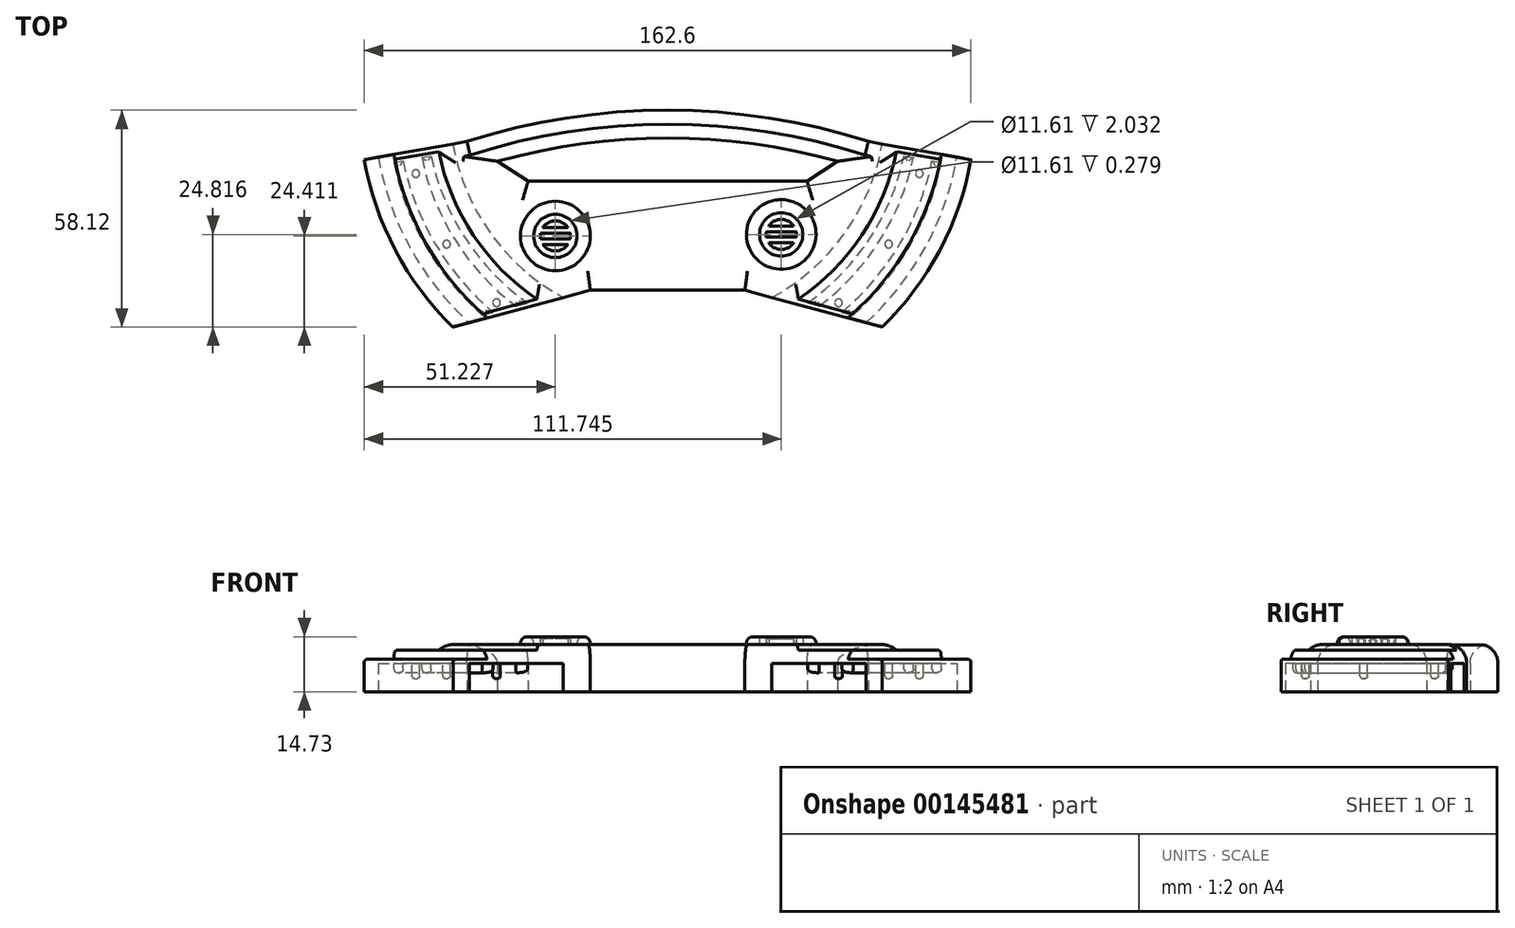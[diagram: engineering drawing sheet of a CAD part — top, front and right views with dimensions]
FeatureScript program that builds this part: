
annotation { "Feature Type Name" : "Feature", "Feature Type Description" : "" }
export const myFeature = defineFeature(function(context is Context, id is Id, definition is map)
    precondition{}
    {
        {
            var Q0;
            Q0=qCreatedBy(makeId("Top.planeOp"),FACE);
            var sketch = newSketch(context, id + "F0", { "sketchPlane" : qUnion([Q0])});
            skCircle(sketch, "E0", {"center": v(0, 0) * mm, "radius": 76.2 * mm, "construction": true});
            skCircle(sketch, "E1", {"center": v(0, 0) * mm, "radius": 60.96 * mm, "construction": true});
            skArc(sketch, "E2", {"start": v(-81.3, -14.33) * mm, "mid": v(-72.94, -38.65) * mm, "end": v(-57.5, -59.22) * mm});
            skLineSegment(sketch, "E3", {"start": v(0, 0) * mm, "end": v(-81.3, -14.33) * mm, "construction": true});
            skArc(sketch, "E4", {"start": v(81.3, -14.33) * mm, "mid": v(72.94, -38.65) * mm, "end": v(57.5, -59.22) * mm});
            skLineSegment(sketch, "E5", {"start": v(81.3, -14.33) * mm, "end": v(0, 0) * mm, "construction": true});
            skLineSegment(sketch, "E6", {"start": v(81.3, -14.33) * mm, "end": v(57.5, -59.22) * mm, "construction": true});
            skLineSegment(sketch, "E7", {"start": v(-81.3, -14.33) * mm, "end": v(-57.5, -59.22) * mm, "construction": true});
            skLineSegment(sketch, "E8", {"start": v(57.5, -59.22) * mm, "end": v(20.7, -49.36) * mm});
            skLineSegment(sketch, "E9", {"start": v(20.7, -49.36) * mm, "end": v(-20.7, -49.36) * mm});
            skLineSegment(sketch, "E10", {"start": v(-20.7, -49.36) * mm, "end": v(-57.5, -59.22) * mm});
            skLineSegment(sketch, "E11", {"start": v(-81.3, -14.33) * mm, "end": v(-53.78, -9.48) * mm});
            skLineSegment(sketch, "E12", {"start": v(-45.58, -14.8) * mm, "end": v(-37.38, -20.13) * mm});
            skLineSegment(sketch, "E13", {"start": v(-37.38, -20.13) * mm, "end": v(37.38, -20.13) * mm});
            skLineSegment(sketch, "E14", {"start": v(37.38, -20.13) * mm, "end": v(45.58, -14.8) * mm});
            skLineSegment(sketch, "E15", {"start": v(53.78, -9.48) * mm, "end": v(81.3, -14.33) * mm});
            skLineSegment(sketch, "E16", {"start": v(0, 0) * mm, "end": v(0, -177.8) * mm, "construction": true});
            skArc(sketch, "E17", {"start": v(-53.78, -9.48) * mm, "mid": v(0, -1.1) * mm, "end": v(53.78, -9.48) * mm});
            skArc(sketch, "E18", {"start": v(45.58, -14.8) * mm, "mid": v(0, -8.56) * mm, "end": v(-45.58, -14.8) * mm});
            skSolve(sketch);
        }
        {
            var Q0;
            Q0=qSketchRegion(id+"F0",true);
            extrude(context, id + "F1", {"entities" : qUnion([Q0]), "depth" : 12.7 * mm});
        }
        {
            var Q0;
            Q0=qCreatedBy(makeId("Front.planeOp"),FACE);
            var sketch = newSketch(context, id + "F2", { "sketchPlane" : qUnion([Q0])});
            skLineSegment(sketch, "E19", {"start": v(62.5, 16.37) * mm, "end": v(62.5, 11.1) * mm});
            skLineSegment(sketch, "E20", {"start": v(62.5, 11.1) * mm, "end": v(74.5, 11.1) * mm});
            skLineSegment(sketch, "E21", {"start": v(74.5, 11.1) * mm, "end": v(74.5, 8.65) * mm});
            skLineSegment(sketch, "E22", {"start": v(74.5, 8.65) * mm, "end": v(83.99, 8.65) * mm});
            skLineSegment(sketch, "E23", {"start": v(83.99, 8.65) * mm, "end": v(83.99, 15.75) * mm});
            skLineSegment(sketch, "E24", {"start": v(83.99, 15.75) * mm, "end": v(62.5, 16.37) * mm});
            skSolve(sketch);
        }
        {
            var Q0;
            Q0=qCreatedBy(makeId("Front.planeOp"),FACE);
            var sketch = newSketch(context, id + "F3", { "sketchPlane" : qUnion([Q0])});
            skLineSegment(sketch, "E25", {"start": v(0, 99.5) * mm, "end": v(0, -112.08) * mm, "construction": true});
            skSolve(sketch);
        }
        {
            var Q0;
            Q0=qSketchRegion(id+"F2",true);
            var Q1;
            Q1=sQuery(id+"F3.wireOp",EDGE,"E25");
            revolve(context, id + "F4", {"operationType" : NewBodyOperationType.REMOVE, "entities" : qUnion([Q0]), "axis" : qUnion([Q1]), "revolveType" : RevolveType.FULL, "oppositeDirection" : true});
        }
        {
            var Q0;
            Q0=makeQuery(id+"F1.opExtrude","CAP_FACE",FACE,{"disambiguationData":[OSD([sQuery(id+"F0.wireOp",EDGE,"E2"),sQuery(id+"F0.wireOp",EDGE,"E4"),sQuery(id+"F0.wireOp",EDGE,"E8"),sQuery(id+"F0.wireOp",EDGE,"E9"),sQuery(id+"F0.wireOp",EDGE,"E10"),sQuery(id+"F0.wireOp",EDGE,"E11"),sQuery(id+"F0.wireOp",EDGE,"E12"),sQuery(id+"F0.wireOp",EDGE,"E13"),sQuery(id+"F0.wireOp",EDGE,"E14"),sQuery(id+"F0.wireOp",EDGE,"E15"),sQuery(id+"F0.wireOp",EDGE,"E17"),sQuery(id+"F0.wireOp",EDGE,"E18")])],"isStart":false});
            fillet(context, id + "F5", {"entities" : qUnion([Q0]), "radius" : 5.08 * mm, "tangentPropagation" : true, "allowEdgeOverflow" : false});
        }
        {
            var Q0;
            Q0=makeQuery(id+"F1.opExtrude","CAP_FACE",FACE,{"disambiguationData":[OSD([sQuery(id+"F0.wireOp",EDGE,"E2"),sQuery(id+"F0.wireOp",EDGE,"E4"),sQuery(id+"F0.wireOp",EDGE,"E8"),sQuery(id+"F0.wireOp",EDGE,"E9"),sQuery(id+"F0.wireOp",EDGE,"E10"),sQuery(id+"F0.wireOp",EDGE,"E11"),sQuery(id+"F0.wireOp",EDGE,"E12"),sQuery(id+"F0.wireOp",EDGE,"E13"),sQuery(id+"F0.wireOp",EDGE,"E14"),sQuery(id+"F0.wireOp",EDGE,"E15"),sQuery(id+"F0.wireOp",EDGE,"E17"),sQuery(id+"F0.wireOp",EDGE,"E18")])],"isStart":false});
            var sketch = newSketch(context, id + "F6", { "sketchPlane" : qUnion([Q0])});
            skLineSegment(sketch, "E26", {"start": v(38.88, -25.21) * mm, "end": v(34.33, -47.75) * mm, "construction": true});
            skLineSegment(sketch, "E27", {"start": v(34.33, -47.75) * mm, "end": v(56.82, -15.18) * mm, "construction": true});
            skLineSegment(sketch, "E28", {"start": v(56.82, -15.18) * mm, "end": v(-56.82, -15.18) * mm, "construction": true});
            skLineSegment(sketch, "E29", {"start": v(-56.82, -15.18) * mm, "end": v(-34.33, -47.75) * mm, "construction": true});
            skLineSegment(sketch, "E30", {"start": v(-34.33, -47.75) * mm, "end": v(-38.88, -25.21) * mm, "construction": true});
            skLineSegment(sketch, "E31", {"start": v(-38.88, -25.21) * mm, "end": v(46.13, -36.48) * mm, "construction": true});
            skPoint(sketch, "E31.endSnap0", {"position": v(-36.6, -36.48) * mm});
            skLineSegment(sketch, "E32", {"start": v(46.13, -36.48) * mm, "end": v(-42.1, -36.48) * mm, "construction": true});
            skLineSegment(sketch, "E33", {"start": v(-42.1, -36.48) * mm, "end": v(38.88, -25.21) * mm, "construction": true});
            skLineSegment(sketch, "E34", {"start": v(21.38, -44.28) * mm, "end": v(38.88, -25.21) * mm, "construction": true});
            skLineSegment(sketch, "E35", {"start": v(-21.38, -44.28) * mm, "end": v(-38.88, -25.21) * mm, "construction": true});
            skCircle(sketch, "E36", {"center": v(30.44, -34.4) * mm, "radius": 9.33 * mm});
            skCircle(sketch, "E37", {"center": v(-30.07, -34.8) * mm, "radius": 9.33 * mm});
            skCircle(sketch, "E38", {"center": v(-30.07, -34.8) * mm, "radius": 5.8 * mm});
            skCircle(sketch, "E39", {"center": v(30.44, -34.4) * mm, "radius": 5.8 * mm});
            skSolve(sketch);
        }
        {
            var Q0;
            Q0=qSketchRegion(id+"F6",true);
            extrude(context, id + "F7", {"entities" : qUnion([Q0]), "operationType" : NewBodyOperationType.ADD, "depth" : 2.03 * mm});
        }
        {
            var Q0;
            Q0=makeQuery(id+"F7.opExtrude","CAP_FACE",FACE,{"disambiguationData":[OSD([sQuery(id+"F6.wireOp",EDGE,"E37"),sQuery(id+"F6.wireOp",EDGE,"E38")])],"isStart":false});
            var Q1;
            Q1=makeQuery(id+"F7.opExtrude","CAP_EDGE",EDGE,{"disambiguationData":[OSD([sQuery(id+"F6.wireOp",EDGE,"E36")])],"isStart":false});
            fillet(context, id + "F8", {"entities" : qUnion([Q0, Q1]), "radius" : 1.75 * mm, "tangentPropagation" : true, "allowEdgeOverflow" : false});
        }
        {
            var Q0;
            Q0=makeQuery(id+"F7.boolean.opBoolean","SPLIT",FACE,{"disambiguationData":[TD([makeQuery(id+"F7.opExtrude","SWEPT_FACE",FACE,{"disambiguationData":[OSD([sQuery(id+"F6.wireOp",EDGE,"E38")])]})])],"derivedFrom":makeQuery(id+"F1.opExtrude","CAP_FACE",FACE,{"disambiguationData":[OSD([sQuery(id+"F0.wireOp",EDGE,"E2"),sQuery(id+"F0.wireOp",EDGE,"E4"),sQuery(id+"F0.wireOp",EDGE,"E8"),sQuery(id+"F0.wireOp",EDGE,"E9"),sQuery(id+"F0.wireOp",EDGE,"E10"),sQuery(id+"F0.wireOp",EDGE,"E11"),sQuery(id+"F0.wireOp",EDGE,"E12"),sQuery(id+"F0.wireOp",EDGE,"E13"),sQuery(id+"F0.wireOp",EDGE,"E14"),sQuery(id+"F0.wireOp",EDGE,"E15"),sQuery(id+"F0.wireOp",EDGE,"E17"),sQuery(id+"F0.wireOp",EDGE,"E18")])],"isStart":false})});
            var sketch = newSketch(context, id + "F9", { "sketchPlane" : qUnion([Q0])});
            skArc(sketch, "E40", {"start": v(-34.04, -34.07) * mm, "mid": v(-34.11, -34.8) * mm, "end": v(-34.04, -35.55) * mm});
            skLineSegment(sketch, "E41", {"start": v(-26.73, -32.55) * mm, "end": v(-33.42, -32.55) * mm});
            skLineSegment(sketch, "E42", {"start": v(-26.1, -34.07) * mm, "end": v(-34.04, -34.07) * mm});
            skLineSegment(sketch, "E43", {"start": v(-26.1, -35.55) * mm, "end": v(-34.04, -35.55) * mm});
            skLineSegment(sketch, "E44", {"start": v(-33.42, -37.07) * mm, "end": v(-26.73, -37.07) * mm});
            skArc(sketch, "E45.trimOffspring", {"start": v(-26.73, -32.55) * mm, "mid": v(-30.07, -30.77) * mm, "end": v(-33.42, -32.55) * mm});
            skArc(sketch, "E46.trimOffspring", {"start": v(-26.1, -35.55) * mm, "mid": v(-26.03, -34.8) * mm, "end": v(-26.1, -34.07) * mm});
            skArc(sketch, "E47.trimOffspring", {"start": v(-33.42, -37.07) * mm, "mid": v(-30.07, -38.85) * mm, "end": v(-26.73, -37.07) * mm});
            skSolve(sketch);
        }
        {
            var Q0;
            Q0=makeQuery(id+"F7.boolean.opBoolean","SPLIT",FACE,{"disambiguationData":[TD([makeQuery(id+"F7.opExtrude","SWEPT_FACE",FACE,{"disambiguationData":[OSD([sQuery(id+"F6.wireOp",EDGE,"E39")])]})])],"derivedFrom":makeQuery(id+"F1.opExtrude","CAP_FACE",FACE,{"disambiguationData":[OSD([sQuery(id+"F0.wireOp",EDGE,"E2"),sQuery(id+"F0.wireOp",EDGE,"E4"),sQuery(id+"F0.wireOp",EDGE,"E8"),sQuery(id+"F0.wireOp",EDGE,"E9"),sQuery(id+"F0.wireOp",EDGE,"E10"),sQuery(id+"F0.wireOp",EDGE,"E11"),sQuery(id+"F0.wireOp",EDGE,"E12"),sQuery(id+"F0.wireOp",EDGE,"E13"),sQuery(id+"F0.wireOp",EDGE,"E14"),sQuery(id+"F0.wireOp",EDGE,"E15"),sQuery(id+"F0.wireOp",EDGE,"E17"),sQuery(id+"F0.wireOp",EDGE,"E18")])],"isStart":false})});
            var sketch = newSketch(context, id + "F10", { "sketchPlane" : qUnion([Q0])});
            skArc(sketch, "E48", {"start": v(33.8, -32.14) * mm, "mid": v(30.44, -30.37) * mm, "end": v(27.1, -32.14) * mm});
            skLineSegment(sketch, "E49", {"start": v(27.1, -32.14) * mm, "end": v(33.8, -32.14) * mm});
            skLineSegment(sketch, "E50", {"start": v(34.42, -33.67) * mm, "end": v(26.47, -33.67) * mm});
            skLineSegment(sketch, "E51", {"start": v(26.47, -35.14) * mm, "end": v(34.42, -35.14) * mm});
            skLineSegment(sketch, "E52", {"start": v(33.8, -36.67) * mm, "end": v(27.1, -36.67) * mm});
            skArc(sketch, "E53.trimOffspring", {"start": v(26.47, -33.67) * mm, "mid": v(26.4, -34.4) * mm, "end": v(26.47, -35.14) * mm});
            skArc(sketch, "E54.trimOffspring", {"start": v(27.1, -36.67) * mm, "mid": v(30.44, -38.44) * mm, "end": v(33.8, -36.67) * mm});
            skArc(sketch, "E55.trimOffspring", {"start": v(34.42, -35.14) * mm, "mid": v(34.48, -34.4) * mm, "end": v(34.42, -33.67) * mm});
            skSolve(sketch);
        }
        {
            var Q0;
            Q0=qSketchRegion(id+"F9",true);
            extrude(context, id + "F11", {"entities" : qUnion([Q0]), "operationType" : NewBodyOperationType.ADD, "depth" : 1.52 * mm});
        }
        {
            var Q0;
            Q0=makeQuery(id+"F11.opExtrude","CAP_EDGE",EDGE,{"disambiguationData":[OSD([sQuery(id+"F9.wireOp",EDGE,"E42")])],"isStart":false});
            var Q1;
            Q1=makeQuery(id+"F11.opExtrude","CAP_EDGE",EDGE,{"disambiguationData":[OSD([sQuery(id+"F9.wireOp",EDGE,"E43")])],"isStart":false});
            fillet(context, id + "F12", {"entities" : qUnion([Q0, Q1]), "radius" : 0.7 * mm, "tangentPropagation" : true, "allowEdgeOverflow" : false});
        }
        {
            var Q0;
            Q0=makeQuery(id+"F11.opExtrude","CAP_FACE",FACE,{"disambiguationData":[OSD([sQuery(id+"F9.wireOp",EDGE,"E41"),sQuery(id+"F9.wireOp",EDGE,"E45.trimOffspring")])],"isStart":false});
            var Q1;
            Q1=makeQuery(id+"F11.opExtrude","CAP_FACE",FACE,{"disambiguationData":[OSD([sQuery(id+"F9.wireOp",EDGE,"E44"),sQuery(id+"F9.wireOp",EDGE,"E47.trimOffspring")])],"isStart":false});
            fillet(context, id + "F13", {"entities" : qUnion([Q0, Q1]), "radius" : 0.25 * mm, "tangentPropagation" : true, "allowEdgeOverflow" : false});
        }
        {
            var Q0;
            Q0=qSketchRegion(id+"F10",true);
            extrude(context, id + "F14", {"entities" : qUnion([Q0]), "operationType" : NewBodyOperationType.ADD, "depth" : 1.52 * mm});
        }
        {
            var Q0;
            {var subQ0=sQuery(id+"F2.wireOp",EDGE,"E20");var subQ1=sQuery(id+"F2.wireOp",EDGE,"E21");Q0=makeQuery(id+"F4.boolean.opBoolean","COPY",EDGE,{"disambiguationData":[TD([makeQuery(id+"F1.opExtrude","SWEPT_FACE",FACE,{"disambiguationData":[OSD([sQuery(id+"F0.wireOp",EDGE,"E10")])]})])],"derivedFrom":makeQuery(id+"F4.opRevolve","SWEPT_EDGE",EDGE,{"disambiguationData":[OSD([subQ0,subQ1])]})});}
            var Q1;
            Q1=makeQuery(id+"F4.boolean.opBoolean","INTERSECT",EDGE,{"derivedFrom":[makeQuery(id+"F1.opExtrude","SWEPT_FACE",FACE,{"disambiguationData":[OSD([sQuery(id+"F0.wireOp",EDGE,"E2")])]}),makeQuery(id+"F4.opRevolve","SWEPT_FACE",FACE,{"disambiguationData":[OSD([sQuery(id+"F2.wireOp",EDGE,"E22")])]})]});
            var Q2;
            {var subQ0=sQuery(id+"F2.wireOp",EDGE,"E20");var subQ1=sQuery(id+"F2.wireOp",EDGE,"E21");Q2=makeQuery(id+"F4.boolean.opBoolean","COPY",EDGE,{"disambiguationData":[TD([makeQuery(id+"F1.opExtrude","SWEPT_FACE",FACE,{"disambiguationData":[OSD([sQuery(id+"F0.wireOp",EDGE,"E8")])]})])],"derivedFrom":makeQuery(id+"F4.opRevolve","SWEPT_EDGE",EDGE,{"disambiguationData":[OSD([subQ0,subQ1])]})});}
            var Q3;
            Q3=makeQuery(id+"F4.boolean.opBoolean","INTERSECT",EDGE,{"derivedFrom":[makeQuery(id+"F1.opExtrude","SWEPT_FACE",FACE,{"disambiguationData":[OSD([sQuery(id+"F0.wireOp",EDGE,"E4")])]}),makeQuery(id+"F4.opRevolve","SWEPT_FACE",FACE,{"disambiguationData":[OSD([sQuery(id+"F2.wireOp",EDGE,"E22")])]})]});
            fillet(context, id + "F15", {"entities" : qUnion([Q0, Q1, Q2, Q3]), "radius" : 0.76 * mm, "tangentPropagation" : true, "allowEdgeOverflow" : false});
        }
        {
            var Q0;
            Q0=qCreatedBy(makeId("Top.planeOp"),FACE);
            var sketch = newSketch(context, id + "F16", { "sketchPlane" : qUnion([Q0])});
            skCircle(sketch, "E56", {"center": v(0, 0) * mm, "radius": 78.74 * mm});
            skCircle(sketch, "E57", {"center": v(0, 0) * mm, "radius": 58.42 * mm});
            skSolve(sketch);
        }
        {
            var Q0;
            Q0=qSketchRegion(id+"F16",true);
            extrude(context, id + "F17", {"entities" : qUnion([Q0]), "operationType" : NewBodyOperationType.REMOVE, "depth" : 7.62 * mm});
        }
        {
            var Q0;
            Q0=makeQuery(id+"F14.opExtrude","CAP_EDGE",EDGE,{"disambiguationData":[OSD([sQuery(id+"F10.wireOp",EDGE,"E50")])],"isStart":false});
            var Q1;
            Q1=makeQuery(id+"F14.opExtrude","CAP_EDGE",EDGE,{"disambiguationData":[OSD([sQuery(id+"F10.wireOp",EDGE,"E51")])],"isStart":false});
            fillet(context, id + "F18", {"entities" : qUnion([Q0, Q1]), "radius" : 0.71 * mm, "tangentPropagation" : true, "allowEdgeOverflow" : false});
        }
        {
            var Q0;
            Q0=makeQuery(id+"F14.opExtrude","CAP_FACE",FACE,{"disambiguationData":[OSD([sQuery(id+"F10.wireOp",EDGE,"E48"),sQuery(id+"F10.wireOp",EDGE,"E49")])],"isStart":false});
            var Q1;
            Q1=makeQuery(id+"F14.opExtrude","CAP_FACE",FACE,{"disambiguationData":[OSD([sQuery(id+"F10.wireOp",EDGE,"E52"),sQuery(id+"F10.wireOp",EDGE,"E54.trimOffspring")])],"isStart":false});
            fillet(context, id + "F19", {"entities" : qUnion([Q0, Q1]), "radius" : 0.25 * mm, "tangentPropagation" : true, "allowEdgeOverflow" : false});
        }
        {
            var Q0;
            {var subQ1=sQuery(id+"F0.wireOp",EDGE,"E10");var subQ2=sQuery(id+"F16.wireOp",EDGE,"E56");var subQ3=sQuery(id+"F16.wireOp",EDGE,"E57");Q0=makeQuery(id+"F17.boolean.opBoolean","COPY",FACE,{"disambiguationData":[TD([makeQuery(id+"F1.opExtrude","SWEPT_FACE",FACE,{"disambiguationData":[OSD([subQ1])]})])],"derivedFrom":makeQuery(id+"F17.opExtrude","CAP_FACE",FACE,{"disambiguationData":[OSD([subQ2,subQ3])],"isStart":false})});}
            var sketch = newSketch(context, id + "F20", { "sketchPlane" : qUnion([Q0])});
            skCircle(sketch, "E58", {"center": v(0, 0) * mm, "radius": 76.2 * mm, "construction": true});
            skCircle(sketch, "E59", {"center": v(0, 0) * mm, "radius": 60.96 * mm, "construction": true});
            skLineSegment(sketch, "E60", {"start": v(0, 0) * mm, "end": v(67.47, 18.08) * mm, "construction": true});
            skCircle(sketch, "E61", {"center": v(0, 0) * mm, "radius": 69.85 * mm, "construction": true});
            skLineSegment(sketch, "E62", {"start": v(0, 0) * mm, "end": v(59.24, 37.01) * mm, "construction": true});
            skLineSegment(sketch, "E63", {"start": v(0, 0) * mm, "end": v(45.83, 52.72) * mm, "construction": true});
            skCircle(sketch, "E64", {"center": v(67.47, 18.08) * mm, "radius": 1.02 * mm});
            skCircle(sketch, "E65", {"center": v(59.24, 37.01) * mm, "radius": 1.02 * mm});
            skCircle(sketch, "E66", {"center": v(45.83, 52.72) * mm, "radius": 1.02 * mm});
            skCircle(sketch, "E67.MirrorC", {"center": v(-67.47, 18.08) * mm, "radius": 1.02 * mm});
            skCircle(sketch, "E68.MirrorC", {"center": v(-59.24, 37.01) * mm, "radius": 1.02 * mm});
            skCircle(sketch, "E69.MirrorC", {"center": v(-45.83, 52.72) * mm, "radius": 1.02 * mm});
            skSolve(sketch);
        }
        {
            var Q0;
            Q0=qSketchRegion(id+"F20",true);
            extrude(context, id + "F21", {"entities" : qUnion([Q0]), "operationType" : NewBodyOperationType.ADD, "depth" : 4.06 * mm});
        }
        {
            var Q0;
            Q0=makeQuery(id+"F21.opExtrude","CAP_EDGE",EDGE,{"disambiguationData":[OSD([sQuery(id+"F20.wireOp",EDGE,"E69.MirrorC")])],"isStart":false});
            var Q1;
            Q1=makeQuery(id+"F21.opExtrude","CAP_EDGE",EDGE,{"disambiguationData":[OSD([sQuery(id+"F20.wireOp",EDGE,"E68.MirrorC")])],"isStart":false});
            var Q2;
            Q2=makeQuery(id+"F21.opExtrude","CAP_FACE",FACE,{"disambiguationData":[OSD([sQuery(id+"F20.wireOp",EDGE,"E67.MirrorC")])],"isStart":false});
            var Q3;
            Q3=makeQuery(id+"F21.opExtrude","CAP_FACE",FACE,{"disambiguationData":[OSD([sQuery(id+"F20.wireOp",EDGE,"E66")])],"isStart":false});
            var Q4;
            Q4=makeQuery(id+"F21.opExtrude","CAP_EDGE",EDGE,{"disambiguationData":[OSD([sQuery(id+"F20.wireOp",EDGE,"E65")])],"isStart":false});
            var Q5;
            Q5=makeQuery(id+"F21.opExtrude","CAP_EDGE",EDGE,{"disambiguationData":[OSD([sQuery(id+"F20.wireOp",EDGE,"E64")])],"isStart":false});
            fillet(context, id + "F22", {"entities" : qUnion([Q0, Q1, Q2, Q3, Q4, Q5]), "radius" : 0.64 * mm, "tangentPropagation" : true, "allowEdgeOverflow" : false});
        }
        {
            var Q0;
            {var subQ1=sQuery(id+"F0.wireOp",EDGE,"E10");var subQ2=sQuery(id+"F16.wireOp",EDGE,"E56");var subQ3=sQuery(id+"F16.wireOp",EDGE,"E57");Q0=makeQuery(id+"F17.boolean.opBoolean","COPY",FACE,{"disambiguationData":[TD([makeQuery(id+"F1.opExtrude","SWEPT_FACE",FACE,{"disambiguationData":[OSD([subQ1])]})])],"derivedFrom":makeQuery(id+"F17.opExtrude","CAP_FACE",FACE,{"disambiguationData":[OSD([subQ2,subQ3])],"isStart":false})});}
            var sketch = newSketch(context, id + "F23", { "sketchPlane" : qUnion([Q0])});
            skArc(sketch, "E70", {"start": v(-40.66, 53.64) * mm, "mid": v(-56.87, 36) * mm, "end": v(-65.88, 13.82) * mm});
            skArc(sketch, "E71", {"start": v(-37.52, 52.8) * mm, "mid": v(-54.16, 35.52) * mm, "end": v(-63.37, 13.37) * mm});
            skArc(sketch, "E72", {"start": v(-46.75, 55.27) * mm, "mid": v(-62.21, 37.01) * mm, "end": v(-70.88, 14.7) * mm});
            skArc(sketch, "E73", {"start": v(-49.71, 56.07) * mm, "mid": v(-64.86, 37.52) * mm, "end": v(-73.38, 15.15) * mm});
            skLineSegment(sketch, "E74", {"start": v(-53.19, 58.06) * mm, "end": v(-14.7, 47.75) * mm, "construction": true});
            skLineSegment(sketch, "E75.MirrorCS", {"start": v(53.19, 58.06) * mm, "end": v(14.7, 47.75) * mm, "construction": true});
            skLineSegment(sketch, "E76", {"start": v(-77.54, 13.67) * mm, "end": v(-57.53, 10.14) * mm, "construction": true});
            skLineSegment(sketch, "E77.MirrorCS", {"start": v(77.54, 13.67) * mm, "end": v(57.53, 10.14) * mm, "construction": true});
            skArc(sketch, "E78.trimOffspring", {"start": v(65.88, 13.82) * mm, "mid": v(56.87, 36) * mm, "end": v(40.66, 53.64) * mm});
            skArc(sketch, "E79.trimOffspring", {"start": v(63.37, 13.37) * mm, "mid": v(54.16, 35.52) * mm, "end": v(37.52, 52.8) * mm});
            skArc(sketch, "E80.trimOffspring", {"start": v(73.38, 15.15) * mm, "mid": v(64.86, 37.52) * mm, "end": v(49.71, 56.07) * mm});
            skArc(sketch, "E81.trimOffspring", {"start": v(70.88, 14.7) * mm, "mid": v(62.21, 37.01) * mm, "end": v(46.75, 55.27) * mm});
            skLineSegment(sketch, "E82", {"start": v(-54.08, 57.23) * mm, "end": v(-15.24, 46.83) * mm, "construction": true});
            skLineSegment(sketch, "E83", {"start": v(-77.13, 15.82) * mm, "end": v(-46.34, 10.34) * mm, "construction": true});
            skLineSegment(sketch, "E84.MirrorCS", {"start": v(54.08, 57.23) * mm, "end": v(15.24, 46.83) * mm, "construction": true});
            skLineSegment(sketch, "E85.MirrorCS", {"start": v(77.13, 15.82) * mm, "end": v(46.34, 10.34) * mm, "construction": true});
            skLineSegment(sketch, "E86", {"start": v(-49.71, 56.07) * mm, "end": v(-46.75, 55.27) * mm});
            skLineSegment(sketch, "E87", {"start": v(-40.66, 53.64) * mm, "end": v(-37.52, 52.8) * mm});
            skLineSegment(sketch, "E88", {"start": v(-73.38, 15.15) * mm, "end": v(-70.88, 14.7) * mm});
            skLineSegment(sketch, "E89", {"start": v(-65.88, 13.82) * mm, "end": v(-63.37, 13.37) * mm});
            skLineSegment(sketch, "E90", {"start": v(63.37, 13.37) * mm, "end": v(65.88, 13.82) * mm});
            skLineSegment(sketch, "E91", {"start": v(70.88, 14.7) * mm, "end": v(73.38, 15.15) * mm});
            skLineSegment(sketch, "E92", {"start": v(37.52, 52.8) * mm, "end": v(40.66, 53.64) * mm});
            skLineSegment(sketch, "E93", {"start": v(46.75, 55.27) * mm, "end": v(49.71, 56.07) * mm});
            skSolve(sketch);
        }
        {
            var Q0;
            Q0=qSketchRegion(id+"F23",true);
            extrude(context, id + "F24", {"entities" : qUnion([Q0]), "operationType" : NewBodyOperationType.ADD, "depth" : 2.54 * mm});
        }
        {
            var Q0;
            Q0=makeQuery(id+"F24.opExtrude","CAP_FACE",FACE,{"disambiguationData":[OSD([sQuery(id+"F23.wireOp",EDGE,"E78.trimOffspring"),sQuery(id+"F23.wireOp",EDGE,"E79.trimOffspring"),sQuery(id+"F23.wireOp",EDGE,"E90"),sQuery(id+"F23.wireOp",EDGE,"E92")])],"isStart":false});
            var Q1;
            Q1=makeQuery(id+"F24.opExtrude","CAP_FACE",FACE,{"disambiguationData":[OSD([sQuery(id+"F23.wireOp",EDGE,"E80.trimOffspring"),sQuery(id+"F23.wireOp",EDGE,"E81.trimOffspring"),sQuery(id+"F23.wireOp",EDGE,"E91"),sQuery(id+"F23.wireOp",EDGE,"E93")])],"isStart":false});
            var Q2;
            Q2=makeQuery(id+"F24.opExtrude","CAP_FACE",FACE,{"disambiguationData":[OSD([sQuery(id+"F23.wireOp",EDGE,"E72"),sQuery(id+"F23.wireOp",EDGE,"E73"),sQuery(id+"F23.wireOp",EDGE,"E86"),sQuery(id+"F23.wireOp",EDGE,"E88")])],"isStart":false});
            var Q3;
            Q3=makeQuery(id+"F24.opExtrude","CAP_FACE",FACE,{"disambiguationData":[OSD([sQuery(id+"F23.wireOp",EDGE,"E70"),sQuery(id+"F23.wireOp",EDGE,"E71"),sQuery(id+"F23.wireOp",EDGE,"E87"),sQuery(id+"F23.wireOp",EDGE,"E89")])],"isStart":false});
            fillet(context, id + "F25", {"entities" : qUnion([Q0, Q1, Q2, Q3]), "radius" : 1.02 * mm, "tangentPropagation" : true, "allowEdgeOverflow" : false});
        }
    });
